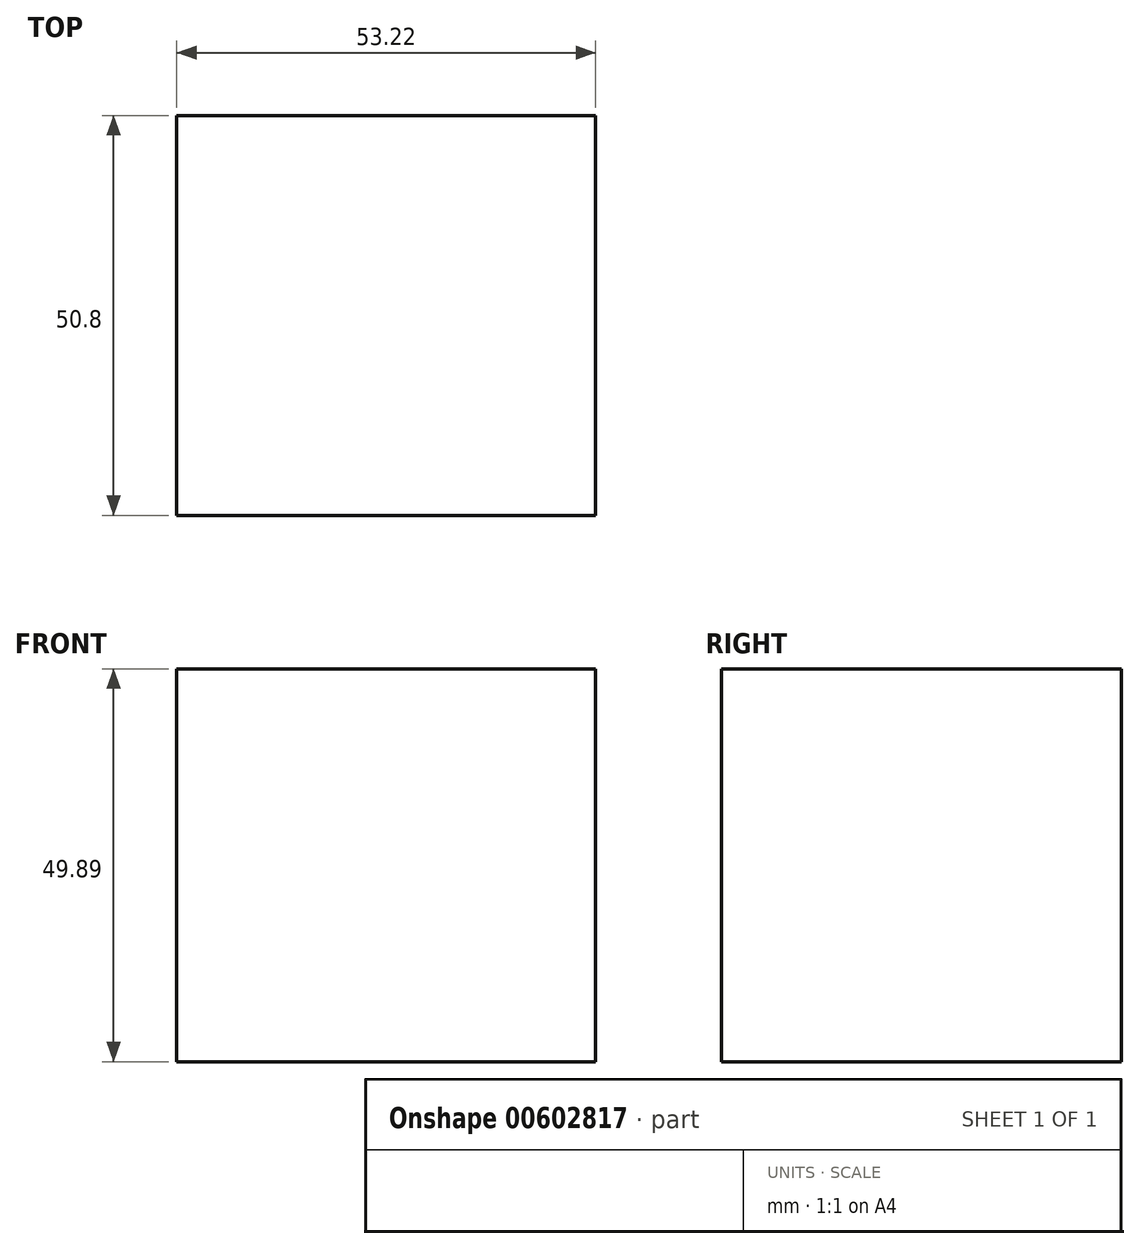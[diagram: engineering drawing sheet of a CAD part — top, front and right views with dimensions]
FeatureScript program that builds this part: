
annotation { "Feature Type Name" : "Feature", "Feature Type Description" : "" }
export const myFeature = defineFeature(function(context is Context, id is Id, definition is map)
    precondition{}
    {
        {
            var Q0;
            Q0=qCreatedBy(makeId("Front.planeOp"),FACE);
            var sketch = newSketch(context, id + "F0", { "sketchPlane" : qUnion([Q0])});
            skSolve(sketch);
        }
        {
            var Q0;
            Q0=qCreatedBy(makeId("Front.planeOp"),FACE);
            var sketch = newSketch(context, id + "F1", { "sketchPlane" : qUnion([Q0])});
            skLineSegment(sketch, "E0.bottom", {"start": v(0, 49.89) * mm, "end": v(53.22, 49.89) * mm});
            skLineSegment(sketch, "E0.top", {"start": v(0, 0) * mm, "end": v(53.22, 0) * mm});
            skLineSegment(sketch, "E0.left", {"start": v(0, 49.89) * mm, "end": v(0, 0) * mm});
            skLineSegment(sketch, "E0.right", {"start": v(53.22, 49.89) * mm, "end": v(53.22, 0) * mm});
            skSolve(sketch);
        }
        {
            var Q0;
            Q0=qSketchRegion(id+"F1",true);
            var Q1;
            Q1=qSketchRegion(id+"F0",true);
            extrude(context, id + "F2", {"entities" : qUnion([Q0, Q1]), "depth" : 50.8 * mm, "offsetDistance" : 25.4 * mm});
        }
    });
